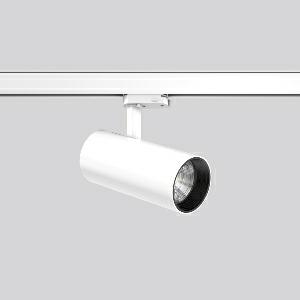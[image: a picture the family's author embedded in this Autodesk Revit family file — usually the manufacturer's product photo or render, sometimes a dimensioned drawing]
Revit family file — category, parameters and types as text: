
# Revit family: deecos_s_mini_742207_002_3_8de8
name_source: partatom
category: Lighting Fixtures
units: mm (PartAtom-declared; Revit-internal decimal feet)

## family parameters
Cut with Voids When Loaded = No
Host = Face
Light Source = No
Part Type = Normal
Room Calculation Point = No
Round Connector Dimension = Use Diameter
Shared = No

## types (1)
- DEECOS S mini (1 x LED Modul 935, 3050 lm, 3500)
    Apparent Load = 29 VA
    Approval mark = CE
    CIE Flux Codes = 96 100 100 100 100
    Color Rendering = 92
    Color Temperature = 3500
    Default Elevation = 1800 mm
    Description = Series: DEECOS S mini
LED surface-mounted projector in modern design with no visible cooling ribs. Housing: die-cast aluminium, powder-coated. Rotation range: 356°. Swivel range: 90°. Black plastic ring and recessed LED to prevent glare from the side. Optical assembly with lens made of plastic (polycarbonate) for the best homogeneous light distribution - can be changed without tools. Best colour rendering index Ra>90. With multi adaptor for 3-circuit tracks 230 V. Suitable for Track on ceiling, Wall track. High quality converter without flickering and stroboscopic effect. The following accessories can be mounted without use of tools: interchangeable lenses, decorative glasses, honeycomb louvre, clear and frosted diffusers, white interchangeable plastic ring. 
Colour: traffic white, matt (RAL 9016)
Diameter: 87 mm
Height: 214 mm
Lamp: LED
Socket: without socket
Colour temperature: 3500K
Colour rendering index (CRI): 92
System power: 29 W
Rated luminous flux: 3050 lm
Luminous efficiency: 105 lm/W
Control gear: Regulated power supply
Protection class: I
Type of protection: IP 20
    Height = 214 mm
    Lamp = 1 x LED Modul 935
    Lamp Light Flux = 3050 lm
    Lamp count = 1
    Length = 87 mm
    Lifetime = 50000 h
    Luminous efficacy = 105 lm/W
    Manufacturer = RZB
    ModVariant = No
    Model = 742207.002.3
    Mounting Place = Ceiling
    Mounting Type = Rail mounted
    Number of Poles = 1
    OnlyDefault = Yes
    Power Factor = 1
    Product Name = DEECOS S mini
    Product group = Track mounted projectors
    ProductGroupID = 301
    Protection Class = Protection class I
    Protection Degree = IP 20
    RLX_Detail_Level = 1
    RLX_Emergency_Light_Flux = 0 lm
    RLX_Emergency_Type = 0
    RLX_Emergency_Type_DB = No
    RlxData = <blob elided: 35345 chars, md5=a8c41755>
    Socket = socket
    Standby Power = 0 W
    System Light Flux = 3050 lm
    System Power = 29 W
    Type Comments = Product without accessories
    Type Image = 741930.002.jpg
    URL = http://relux.com
    VarID = ---
    Voltage = 230 V
    Voltage Range = 220-240 V
    Weight = 0.00 kg
    Width = 0 mm  [stored 0 ft]

note: [stored X ft] marks values corroborated as IEEE doubles in the binary element streams (Revit-internal decimal feet)

## geometry (parser evidence)
native form markers: Blend x4, Sweep x12
no freeform markers — native parametric forms only
